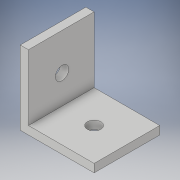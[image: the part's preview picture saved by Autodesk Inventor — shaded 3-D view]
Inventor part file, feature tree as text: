
AUTODESK INVENTOR PART (.ipt)
format: ipt  version: 2019 (Build 230136000, 136)  size: 122,880 bytes
history: native  units: in
note: dims shown in document units (in); Inventor stores cm internally (conversion verified against a paired STEP export)
features: extrude x4, sketch x4
ambient origin geometry x8: Origin, YZ Plane, XZ Plane, XY Plane, X Axis, Y Axis, Z Axis, Center Point
bodies: Solid1 (feature_tree)
feature tree (8):
  extrude  "Extrusion1"  Depth=1.0in
  extrude  "Extrusion2"  Depth=0.125in
  sketch  "Sketch3"  dims[d5=0.5in d6=0.125in]
  extrude  "Extrusion3"  Depth=0.125in
  extrude  "Extrusion4"  Depth=1.125in
  sketch  "Sketch1"  dims[d0=1.0in d1=1.0in]
  sketch  "Sketch2"  dims[d2=0.125in d3=0.0in d4=0.5in]
  sketch  "Sketch4"  dims[d7=1.125in d8=0.0in d9=0.2031in d10=0.2031in d11=1.125in d12=0.0in d13=1.125in d14=0.0in]
